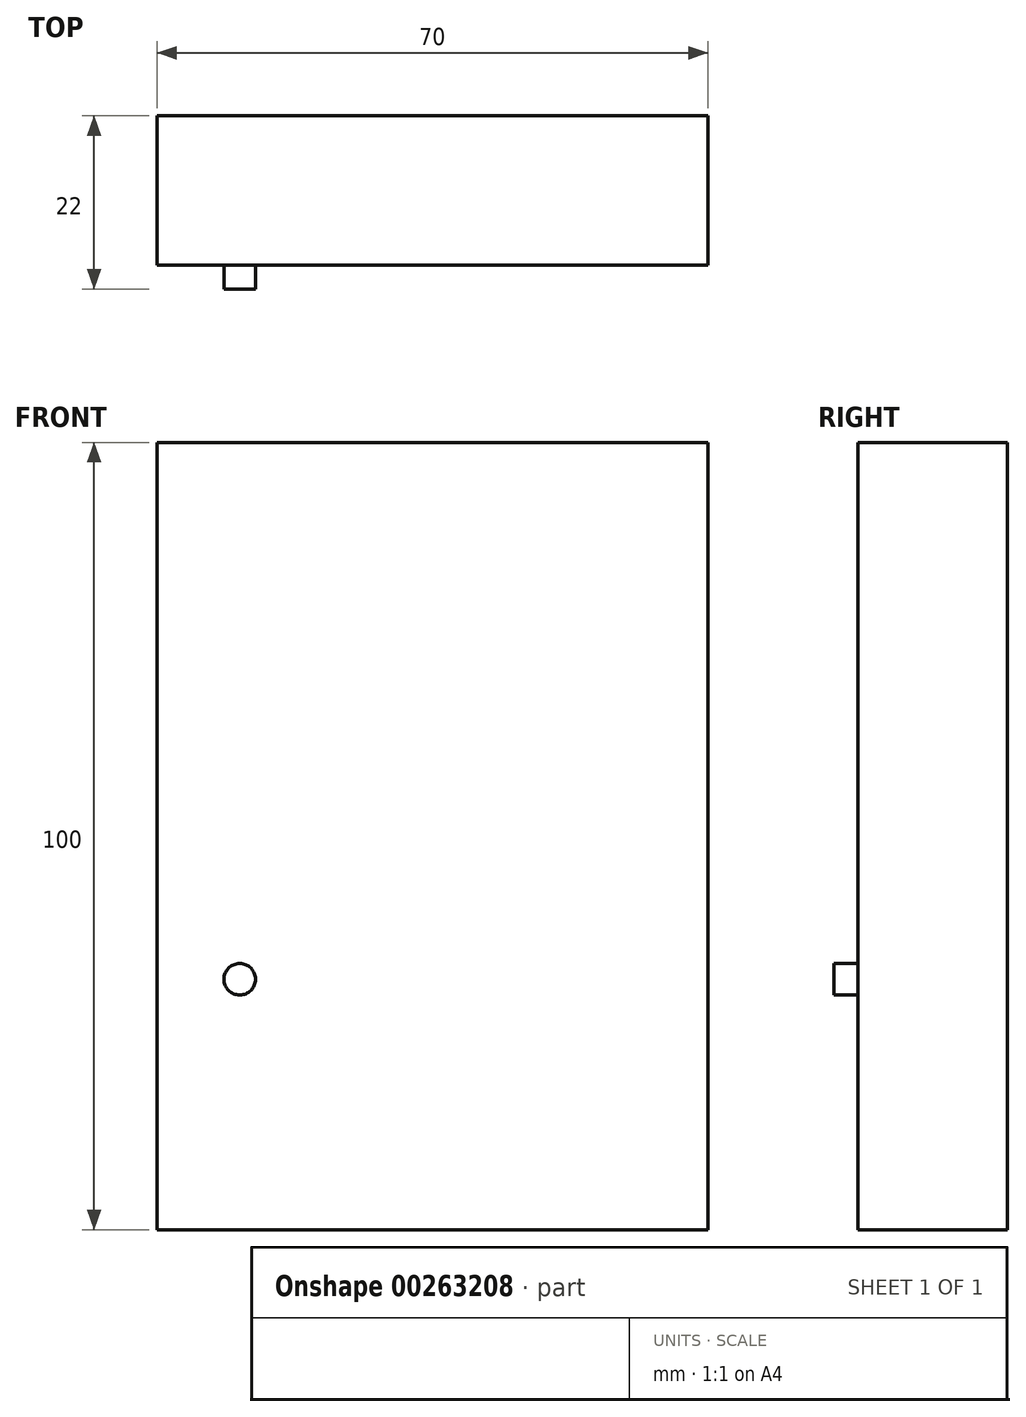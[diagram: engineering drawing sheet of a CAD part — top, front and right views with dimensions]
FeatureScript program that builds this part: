
annotation { "Feature Type Name" : "Feature", "Feature Type Description" : "" }
export const myFeature = defineFeature(function(context is Context, id is Id, definition is map)
    precondition{}
    {
        {
            var Q0;
            Q0=qCreatedBy(makeId("Front.planeOp"),FACE);
            var sketch = newSketch(context, id + "F0", { "sketchPlane" : qUnion([Q0])});
            skLineSegment(sketch, "E0.bottom", {"start": v(0, 0) * mm, "end": v(70, 0) * mm});
            skLineSegment(sketch, "E0.top", {"start": v(0, -100) * mm, "end": v(70, -100) * mm});
            skLineSegment(sketch, "E0.left", {"start": v(0, 0) * mm, "end": v(0, -100) * mm});
            skLineSegment(sketch, "E0.right", {"start": v(70, 0) * mm, "end": v(70, -100) * mm});
            skSolve(sketch);
        }
        {
            var Q0;
            Q0=makeQuery(id+"F0.imprint","IMPRINT",FACE,{"disambiguationData":[TD([[makeQuery(id+"F0.imprint","IMPRINT",EDGE,{"derivedFrom":sQuery(id+"F0.wireOp",EDGE,"E0.bottom")}),-1.0]])]});
            extrude(context, id + "F1", {"entities" : qUnion([Q0]), "depth" : 19 * mm});
        }
        {
            var Q0;
            Q0=makeQuery(id+"F1.opExtrude","CAP_FACE",FACE,{"disambiguationData":[OSD([sQuery(id+"F0.wireOp",EDGE,"E0.bottom"),sQuery(id+"F0.wireOp",EDGE,"E0.top"),sQuery(id+"F0.wireOp",EDGE,"E0.left"),sQuery(id+"F0.wireOp",EDGE,"E0.right")])],"isStart":false});
            var sketch = newSketch(context, id + "F2", { "sketchPlane" : qUnion([Q0])});
            skLineSegment(sketch, "E1.bottom", {"start": v(12, -8) * mm, "end": v(57, -8) * mm});
            skLineSegment(sketch, "E1.left", {"start": v(8, -11.36) * mm, "end": v(8, -86.34) * mm});
            skLineSegment(sketch, "E1.right", {"start": v(62, -13) * mm, "end": v(62, -88.13) * mm});
            skPoint(sketch, "E2.visualSharp", {"position": v(62, -8) * mm});
            skArc(sketch, "E2.filletArc", {"start": v(62, -13) * mm, "mid": v(60.54, -9.46) * mm, "end": v(57, -8) * mm});
            skLineSegment(sketch, "E3", {"start": v(12, -8) * mm, "end": v(8, -11.36) * mm});
            skPoint(sketch, "E4.visualSharp", {"position": v(62, -87.84) * mm});
            skArc(sketch, "E4.filletArc", {"start": v(59, -92) * mm, "mid": v(61.16, -90.58) * mm, "end": v(62, -88.13) * mm});
            skLineSegment(sketch, "E5", {"start": v(59, -92) * mm, "end": v(13.66, -92) * mm});
            skPoint(sketch, "E6.bottom.start.orphan", {"position": v(8, -88.64) * mm});
            skPoint(sketch, "E6.right.end.orphan", {"position": v(11, -90.6) * mm});
            skLineSegment(sketch, "E7", {"start": v(13.66, -92) * mm, "end": v(8, -86.34) * mm});
            skSolve(sketch);
        }
        {
            var Q0;
            Q0=makeQuery(id+"F2.imprint","IMPRINT",FACE,{"disambiguationData":[TD([[makeQuery(id+"F2.imprint","IMPRINT",EDGE,{"derivedFrom":sQuery(id+"F2.wireOp",EDGE,"E1.bottom")}),-1.0]])]});
            extrude(context, id + "F3", {"entities" : qUnion([Q0]), "operationType" : NewBodyOperationType.ADD, "depth" : 3 * mm});
        }
        {
            var Q0;
            Q0=makeQuery(id+"F3.opExtrude","CAP_FACE",FACE,{"disambiguationData":[OSD([sQuery(id+"F2.wireOp",EDGE,"E1.bottom"),sQuery(id+"F2.wireOp",EDGE,"E1.left"),sQuery(id+"F2.wireOp",EDGE,"E1.right"),sQuery(id+"F2.wireOp",EDGE,"E2.filletArc"),sQuery(id+"F2.wireOp",EDGE,"E3"),sQuery(id+"F2.wireOp",EDGE,"E4.filletArc"),sQuery(id+"F2.wireOp",EDGE,"E5"),sQuery(id+"F2.wireOp",EDGE,"E7")])],"isStart":false});
            var sketch = newSketch(context, id + "F4", { "sketchPlane" : qUnion([Q0])});
            skCircle(sketch, "E8", {"center": v(35, -30) * mm, "radius": 16 * mm});
            skSolve(sketch);
        }
        {
            var Q0;
            Q0=makeQuery(id+"F4.imprint","IMPRINT",FACE,{"disambiguationData":[TD([[makeQuery(id+"F4.imprint","IMPRINT",EDGE,{"derivedFrom":sQuery(id+"F4.wireOp",EDGE,"E8")}),1.0]])]});
            extrude(context, id + "F5", {"entities" : qUnion([Q0]), "operationType" : NewBodyOperationType.REMOVE, "oppositeDirection" : true, "depth" : 3 * mm});
        }
        {
            var Q0;
            Q0=makeQuery(id+"F3.opExtrude","CAP_FACE",FACE,{"disambiguationData":[OSD([sQuery(id+"F2.wireOp",EDGE,"E1.bottom"),sQuery(id+"F2.wireOp",EDGE,"E1.left"),sQuery(id+"F2.wireOp",EDGE,"E1.right"),sQuery(id+"F2.wireOp",EDGE,"E2.filletArc"),sQuery(id+"F2.wireOp",EDGE,"E3"),sQuery(id+"F2.wireOp",EDGE,"E4.filletArc"),sQuery(id+"F2.wireOp",EDGE,"E5"),sQuery(id+"F2.wireOp",EDGE,"E7")])],"isStart":false});
            var sketch = newSketch(context, id + "F6", { "sketchPlane" : qUnion([Q0])});
            skLineSegment(sketch, "E9", {"start": v(29.6, -64.43) * mm, "end": v(47.6, -64.43) * mm});
            skLineSegment(sketch, "E10", {"start": v(53.6, -70.43) * mm, "end": v(53.6, -78.43) * mm});
            skLineSegment(sketch, "E11", {"start": v(23.54, -78.4) * mm, "end": v(23.6, -70.4) * mm});
            skLineSegment(sketch, "E12", {"start": v(29.54, -84.43) * mm, "end": v(47.6, -84.43) * mm});
            skPoint(sketch, "E13.visualSharp", {"position": v(53.6, -64.43) * mm});
            skArc(sketch, "E13.filletArc", {"start": v(53.6, -70.43) * mm, "mid": v(51.83, -66.19) * mm, "end": v(47.6, -64.43) * mm});
            skPoint(sketch, "E14.visualSharp", {"position": v(53.6, -84.43) * mm});
            skArc(sketch, "E14.filletArc", {"start": v(47.6, -84.43) * mm, "mid": v(51.83, -82.67) * mm, "end": v(53.6, -78.43) * mm});
            skPoint(sketch, "E15.visualSharp", {"position": v(23.63, -64.43) * mm});
            skArc(sketch, "E15.filletArc", {"start": v(29.6, -64.43) * mm, "mid": v(25.36, -66.18) * mm, "end": v(23.6, -70.4) * mm});
            skPoint(sketch, "E16.visualSharp", {"position": v(23.5, -84.43) * mm});
            skArc(sketch, "E16.filletArc", {"start": v(23.54, -78.4) * mm, "mid": v(25.29, -82.66) * mm, "end": v(29.54, -84.43) * mm});
            skSolve(sketch);
        }
        {
            var Q0;
            Q0=makeQuery(id+"F6.imprint","IMPRINT",FACE,{"disambiguationData":[TD([[makeQuery(id+"F6.imprint","IMPRINT",EDGE,{"derivedFrom":sQuery(id+"F6.wireOp",EDGE,"E9")}),-1.0]])]});
            extrude(context, id + "F7", {"entities" : qUnion([Q0]), "operationType" : NewBodyOperationType.REMOVE, "oppositeDirection" : true, "depth" : 3 * mm});
        }
        {
            var Q0;
            Q0=makeQuery(id+"F3.opExtrude","CAP_FACE",FACE,{"disambiguationData":[OSD([sQuery(id+"F2.wireOp",EDGE,"E1.bottom"),sQuery(id+"F2.wireOp",EDGE,"E1.left"),sQuery(id+"F2.wireOp",EDGE,"E1.right"),sQuery(id+"F2.wireOp",EDGE,"E2.filletArc"),sQuery(id+"F2.wireOp",EDGE,"E3"),sQuery(id+"F2.wireOp",EDGE,"E4.filletArc"),sQuery(id+"F2.wireOp",EDGE,"E5"),sQuery(id+"F2.wireOp",EDGE,"E7")])],"isStart":false});
            var sketch = newSketch(context, id + "F8", { "sketchPlane" : qUnion([Q0])});
            skCircle(sketch, "E17", {"center": v(10.5, -31.81) * mm, "radius": 2 * mm});
            skCircle(sketch, "E18", {"center": v(18.19, -39.5) * mm, "radius": 2 * mm});
            skCircle(sketch, "E19", {"center": v(21, -50) * mm, "radius": 2 * mm});
            skCircle(sketch, "E20", {"center": v(18.19, -60.5) * mm, "radius": 2 * mm});
            skLineSegment(sketch, "E21", {"start": v(21, -50) * mm, "end": v(0, -50) * mm});
            skLineSegment(sketch, "E22", {"start": v(8, -50) * mm, "end": v(0, -50) * mm});
            skCircle(sketch, "E23.MirrorC", {"center": v(10.5, -68.19) * mm, "radius": 2 * mm});
            skSolve(sketch);
        }
        {
            var Q0;
            Q0=makeQuery(id+"F8.imprint","IMPRINT",FACE,{"disambiguationData":[TD([[makeQuery(id+"F8.imprint","IMPRINT",EDGE,{"derivedFrom":sQuery(id+"F8.wireOp",EDGE,"E17")}),1.0]])]});
            var Q1;
            Q1=makeQuery(id+"F8.imprint","IMPRINT",FACE,{"disambiguationData":[TD([[makeQuery(id+"F8.imprint","IMPRINT",EDGE,{"derivedFrom":sQuery(id+"F8.wireOp",EDGE,"E18")}),1.0]])]});
            var Q2;
            Q2=makeQuery(id+"F8.imprint","IMPRINT",FACE,{"disambiguationData":[TD([[makeQuery(id+"F8.imprint","IMPRINT",EDGE,{"derivedFrom":sQuery(id+"F8.wireOp",EDGE,"E19")}),1.0]])]});
            var Q3;
            Q3=makeQuery(id+"F8.imprint","IMPRINT",FACE,{"disambiguationData":[TD([[makeQuery(id+"F8.imprint","IMPRINT",EDGE,{"derivedFrom":sQuery(id+"F8.wireOp",EDGE,"E20")}),1.0]])]});
            var Q4;
            Q4=makeQuery(id+"F8.imprint","IMPRINT",FACE,{"disambiguationData":[TD([[makeQuery(id+"F8.imprint","IMPRINT",EDGE,{"derivedFrom":sQuery(id+"F8.wireOp",EDGE,"E23.MirrorC")}),-1.0]])]});
            extrude(context, id + "F9", {"entities" : qUnion([Q0, Q1, Q2, Q3, Q4]), "operationType" : NewBodyOperationType.REMOVE, "oppositeDirection" : true, "depth" : 3 * mm});
        }
        {
            var Q0;
            Q0=makeQuery(id+"F3.opExtrude","CAP_FACE",FACE,{"disambiguationData":[OSD([sQuery(id+"F2.wireOp",EDGE,"E1.bottom"),sQuery(id+"F2.wireOp",EDGE,"E1.left"),sQuery(id+"F2.wireOp",EDGE,"E1.right"),sQuery(id+"F2.wireOp",EDGE,"E2.filletArc"),sQuery(id+"F2.wireOp",EDGE,"E3"),sQuery(id+"F2.wireOp",EDGE,"E4.filletArc"),sQuery(id+"F2.wireOp",EDGE,"E5"),sQuery(id+"F2.wireOp",EDGE,"E7")])],"isStart":false});
            var sketch = newSketch(context, id + "F10", { "sketchPlane" : qUnion([Q0])});
            skCircle(sketch, "E24", {"center": v(55.9, -50) * mm, "radius": 2 * mm});
            skCircle(sketch, "E25", {"center": v(56, -40) * mm, "radius": 2 * mm});
            skCircle(sketch, "E26", {"center": v(56, -60) * mm, "radius": 2 * mm});
            skSolve(sketch);
        }
        {
            var Q0;
            Q0=makeQuery(id+"F10.imprint","IMPRINT",FACE,{"disambiguationData":[TD([[makeQuery(id+"F10.imprint","IMPRINT",EDGE,{"derivedFrom":sQuery(id+"F10.wireOp",EDGE,"E25")}),1.0]])]});
            var Q1;
            Q1=makeQuery(id+"F10.imprint","IMPRINT",FACE,{"disambiguationData":[TD([[makeQuery(id+"F10.imprint","IMPRINT",EDGE,{"derivedFrom":sQuery(id+"F10.wireOp",EDGE,"E24")}),1.0]])]});
            var Q2;
            Q2=makeQuery(id+"F10.imprint","IMPRINT",FACE,{"disambiguationData":[TD([[makeQuery(id+"F10.imprint","IMPRINT",EDGE,{"derivedFrom":sQuery(id+"F10.wireOp",EDGE,"E26")}),1.0]])]});
            extrude(context, id + "F11", {"entities" : qUnion([Q0, Q1, Q2]), "operationType" : NewBodyOperationType.REMOVE, "oppositeDirection" : true, "depth" : 3 * mm});
        }
    });
